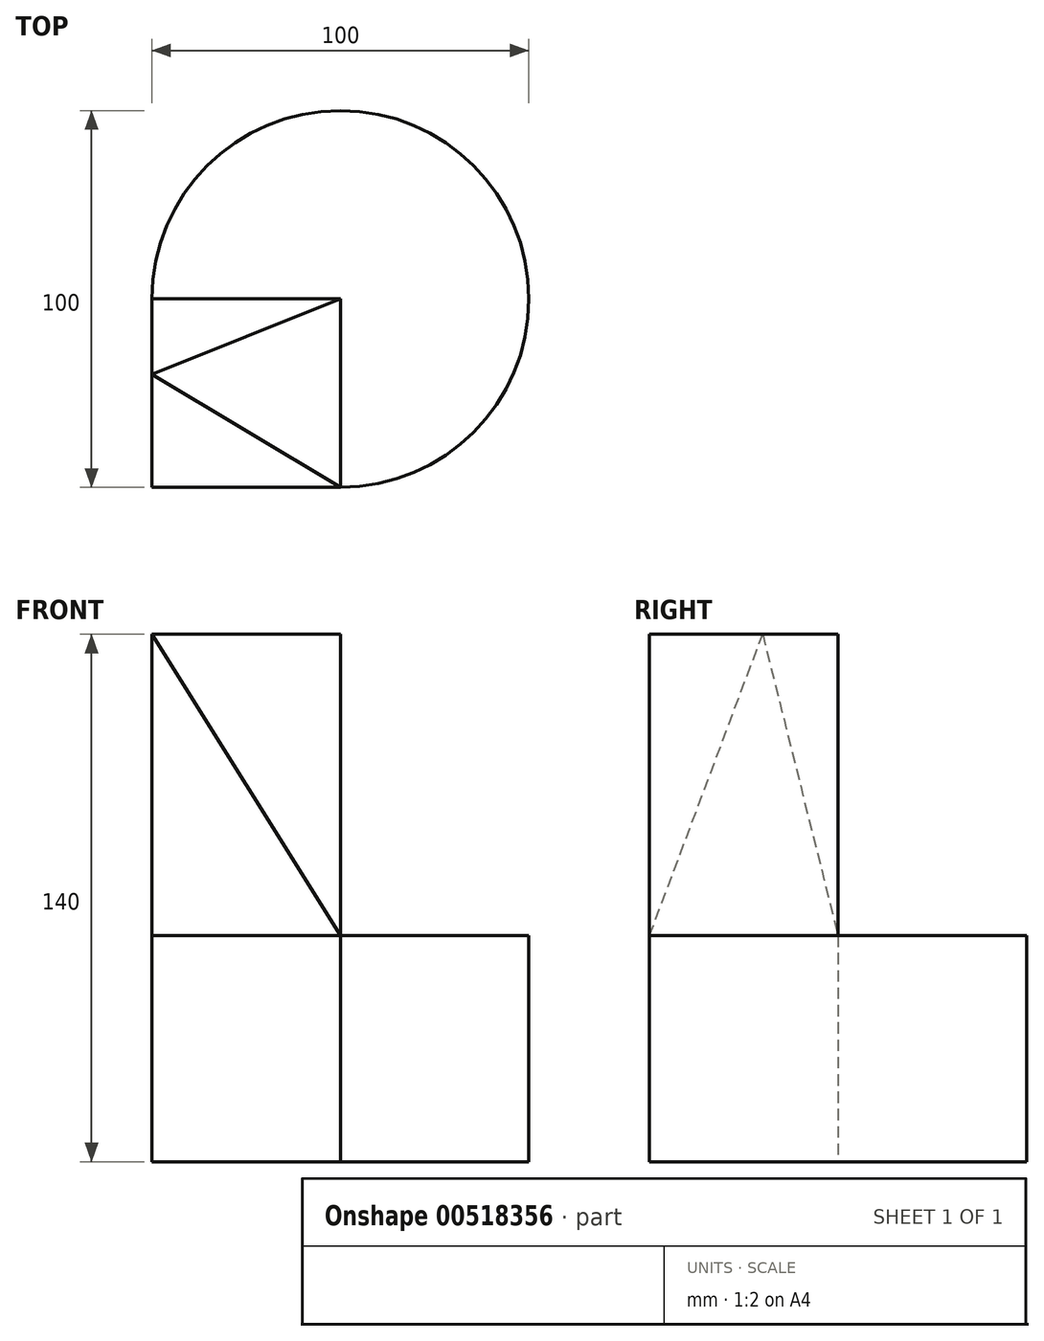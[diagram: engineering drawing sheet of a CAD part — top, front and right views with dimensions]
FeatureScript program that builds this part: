
annotation { "Feature Type Name" : "Feature", "Feature Type Description" : "" }
export const myFeature = defineFeature(function(context is Context, id is Id, definition is map)
    precondition{}
    {
        {
            var Q0;
            Q0=qCreatedBy(makeId("Top.planeOp"),FACE);
            var sketch = newSketch(context, id + "F0", { "sketchPlane" : qUnion([Q0])});
            skCircle(sketch, "E0", {"center": v(0, 0) * mm, "radius": 50 * mm});
            skSolve(sketch);
        }
        {
            var Q0;
            Q0 = qSketchRegion(id + "F0", true);
            extrude(context, id + "F1", {"entities" : qUnion([Q0]), "depth" : 140 * mm, "offsetDistance" : 25 * mm});
        }
        {
            var Q0;
            Q0=makeQuery(id+"F1.opExtrude","CAP_FACE",FACE,{"disambiguationData":[OSD([sQuery(id+"F0.wireOp",EDGE,"E0")])],"isStart":false});
            var sketch = newSketch(context, id + "F2", { "sketchPlane" : qUnion([Q0])});
            skLineSegment(sketch, "E1", {"start": v(0, 0) * mm, "end": v(0, 50) * mm});
            skLineSegment(sketch, "E2", {"start": v(0, 0) * mm, "end": v(0, -50) * mm});
            skSolve(sketch);
        }
        {
            var Q0;
            Q0=makeQuery(id+"F1.opExtrude","CAP_FACE",FACE,{"disambiguationData":[OSD([sQuery(id+"F0.wireOp",EDGE,"E0")])],"isStart":true});
            cPlane(context, id + "F3", {"entities" : qUnion([Q0]), "cplaneType" : CPlaneType.OFFSET, "offset" : 60 * mm, "oppositeDirection" : true, "width" : 150 * mm, "height" : 150 * mm});
        }
        {
            var Q0;
            {var subQ0=sQuery(id+"F2.wireOp",EDGE,"E1");Q0=makeQuery(id+"F2.imprint","IMPRINT",FACE,{"disambiguationData":[TD([[makeQuery(id+"F2.imprint","IMPRINT",EDGE,{"derivedFrom":subQ0}),-1.0]])]});}
            var Q1;
            Q1=qCreatedBy(id+"F3.planeOp",FACE);
            extrude(context, id + "F4", {"entities" : qUnion([Q0]), "operationType" : NewBodyOperationType.REMOVE, "endBound" : BoundingType.UP_TO_SURFACE, "oppositeDirection" : true, "depth" : 25 * mm, "endBoundEntityFace" : qUnion([Q1]), "offsetDistance" : 25 * mm});
        }
        {
            var Q0;
            Q0=makeQuery(id+"F1.opExtrude","CAP_FACE",FACE,{"disambiguationData":[OSD([sQuery(id+"F0.wireOp",EDGE,"E0")])],"isStart":false});
            var sketch = newSketch(context, id + "F5", { "sketchPlane" : qUnion([Q0])});
            skLineSegment(sketch, "E3", {"start": v(0, 0) * mm, "end": v(-50, 0) * mm});
            skSolve(sketch);
        }
        {
            var Q0;
            {var subQ0=sQuery(id+"F5.wireOp",EDGE,"E3");Q0=makeQuery(id+"F5.imprint","IMPRINT",FACE,{"disambiguationData":[TD([[makeQuery(id+"F5.imprint","IMPRINT",EDGE,{"derivedFrom":subQ0}),-1.0]])]});}
            var Q1;
            Q1=qCreatedBy(id+"F3.planeOp",FACE);
            extrude(context, id + "F6", {"entities" : qUnion([Q0]), "operationType" : NewBodyOperationType.REMOVE, "endBound" : BoundingType.UP_TO_SURFACE, "oppositeDirection" : true, "depth" : 25 * mm, "endBoundEntityFace" : qUnion([Q1]), "offsetDistance" : 25 * mm});
        }
        {
            var Q0;
            Q0=makeQuery(id+"F1.opExtrude","CAP_FACE",FACE,{"disambiguationData":[OSD([sQuery(id+"F0.wireOp",EDGE,"E0")])],"isStart":false});
            var Q1;
            Q1=qCreatedBy(id+"F3.planeOp",FACE);
            extrude(context, id + "F7", {"entities" : qUnion([Q0]), "operationType" : NewBodyOperationType.REMOVE, "endBound" : BoundingType.UP_TO_SURFACE, "oppositeDirection" : true, "depth" : 25 * mm, "endBoundEntityFace" : qUnion([Q1]), "offsetDistance" : 25 * mm});
        }
        {
            var Q0;
            {var subQ0=sQuery(id+"F0.wireOp",EDGE,"E0");var subQ1=sQuery(id+"F2.wireOp",EDGE,"E2");var subQ2=sQuery(id+"F2.wireOp",EDGE,"E1");Q0=makeQuery(id+"F7.boolean.opBoolean","MERGE",FACE,{"derivedFrom":[makeQuery(id+"F6.boolean.opBoolean","MERGE",FACE,{"derivedFrom":[makeQuery(id+"F4.boolean.opBoolean","COPY",FACE,{"derivedFrom":makeQuery(id+"F4.opExtrude","CAP_FACE",FACE,{"disambiguationData":[OSD([subQ0,subQ2,subQ1])],"isStart":false})})],"fromTools":[makeQuery(id+"F6.opExtrude","CAP_FACE",FACE,{"disambiguationData":[OSD([subQ0,subQ2,subQ1,sQuery(id+"F5.wireOp",EDGE,"E3")])],"isStart":false})]})],"fromTools":[makeQuery(id+"F7.opExtrude","CAP_FACE",FACE,{"disambiguationData":[OSD([subQ0])],"isStart":false})]});}
            var sketch = newSketch(context, id + "F8", { "sketchPlane" : qUnion([Q0])});
            skLineSegment(sketch, "E4.bottom", {"start": v(0, 0) * mm, "end": v(-50, 0) * mm});
            skLineSegment(sketch, "E4.top", {"start": v(0, -50) * mm, "end": v(-50, -50) * mm});
            skLineSegment(sketch, "E4.left", {"start": v(0, 0) * mm, "end": v(0, -50) * mm});
            skLineSegment(sketch, "E4.right", {"start": v(-50, 0) * mm, "end": v(-50, -50) * mm});
            skSolve(sketch);
        }
        {
            var Q0;
            Q0=makeQuery(id+"F1.opExtrude","CAP_FACE",FACE,{"disambiguationData":[OSD([sQuery(id+"F0.wireOp",EDGE,"E0")])],"isStart":true});
            cPlane(context, id + "F9", {"entities" : qUnion([Q0]), "cplaneType" : CPlaneType.OFFSET, "offset" : 140 * mm, "oppositeDirection" : true, "width" : 150 * mm, "height" : 150 * mm});
        }
        {
            var Q0;
            Q0 = qSketchRegion(id + "F8", true);
            var Q1;
            Q1=qCreatedBy(id+"F9.planeOp",FACE);
            extrude(context, id + "F10", {"entities" : qUnion([Q0]), "operationType" : NewBodyOperationType.ADD, "endBound" : BoundingType.UP_TO_SURFACE, "depth" : 25 * mm, "endBoundEntityFace" : qUnion([Q1]), "offsetDistance" : 25 * mm});
        }
        {
            var Q0;
            Q0=makeQuery(id+"F10.opExtrude","CAP_FACE",FACE,{"disambiguationData":[OSD([sQuery(id+"F8.wireOp",EDGE,"E4.bottom"),sQuery(id+"F8.wireOp",EDGE,"E4.top"),sQuery(id+"F8.wireOp",EDGE,"E4.left"),sQuery(id+"F8.wireOp",EDGE,"E4.right")])],"isStart":false});
            var sketch = newSketch(context, id + "F11", { "sketchPlane" : qUnion([Q0])});
            skLineSegment(sketch, "E5", {"start": v(-50, -20) * mm, "end": v(0, 0) * mm});
            skLineSegment(sketch, "E6", {"start": v(0, 0) * mm, "end": v(0, -50) * mm});
            skLineSegment(sketch, "E7", {"start": v(0, -50) * mm, "end": v(-50, -20) * mm});
            skSolve(sketch);
        }
        {
            var Q0;
            Q0=makeQuery(id+"F10.opExtrude","SWEPT_FACE",FACE,{"disambiguationData":[OSD([sQuery(id+"F8.wireOp",EDGE,"E4.left")])]});
            var sketch = newSketch(context, id + "F12", { "sketchPlane" : qUnion([Q0])});
            skLineSegment(sketch, "E8", {"start": v(-20, 140) * mm, "end": v(-50, 60) * mm});
            skLineSegment(sketch, "E9", {"start": v(-50, 60) * mm, "end": v(0, 60) * mm});
            skLineSegment(sketch, "E10", {"start": v(0, 60) * mm, "end": v(-20, 140) * mm});
            skSolve(sketch);
        }
        {
            var Q1;
            {var subQ0=sQuery(id+"F11.wireOp",EDGE,"E5");Q1=makeQuery(id+"F11.imprint","IMPRINT",FACE,{"disambiguationData":[TD([[makeQuery(id+"F11.imprint","IMPRINT",EDGE,{"derivedFrom":subQ0}),1.0]])]});}
            var Q2;
            Q2=sQuery(id+"F12.wireOp",VERTEX,"E10.start");
            loft(context, id + "F13", {"operationType" : NewBodyOperationType.REMOVE, "sheetProfilesArray" : [{ "sheetProfileEntities" : qUnion([Q1]) }, { "sheetProfileEntities" : qUnion([Q2]) }]});
        }
        {
            var Q1;
            Q1=makeQuery(id+"F10.opExtrude","SWEPT_FACE",FACE,{"disambiguationData":[OSD([sQuery(id+"F8.wireOp",EDGE,"E4.top")])]});
            var Q2;
            Q2=makeQuery(id+"F13.boolean.opBoolean","COPY",VERTEX,{"derivedFrom":makeQuery(id+"F13.opLoft","MID_CAP_VERTEX",VERTEX,{"disambiguationData":[OSD([sQuery(id+"F8.wireOp",EDGE,"E4.right"),dummyQuery(id+"F9.planeOp",FACE),sQuery(id+"F11.wireOp",EDGE,"E5"),sQuery(id+"F11.wireOp",EDGE,"E7")])],"capPos":0.0})});
            loft(context, id + "F14", {"operationType" : NewBodyOperationType.REMOVE, "sheetProfilesArray" : [{ "sheetProfileEntities" : qUnion([Q1]) }, { "sheetProfileEntities" : qUnion([Q2]) }]});
        }
        {
            var Q0;
            Q0=makeQuery(id+"F1.opExtrude","CAP_FACE",FACE,{"disambiguationData":[OSD([sQuery(id+"F0.wireOp",EDGE,"E0")])],"isStart":true});
            var sketch = newSketch(context, id + "F15", { "sketchPlane" : qUnion([Q0])});
            skLineSegment(sketch, "E11", {"start": v(0, 50) * mm, "end": v(0, 0) * mm});
            skLineSegment(sketch, "E12", {"start": v(0, 0) * mm, "end": v(-50, 0) * mm});
            skSolve(sketch);
        }
        {
            var Q0;
            {var subQ0=sQuery(id+"F15.wireOp",EDGE,"E11");Q0=makeQuery(id+"F15.imprint","IMPRINT",FACE,{"disambiguationData":[TD([[makeQuery(id+"F15.imprint","IMPRINT",EDGE,{"derivedFrom":subQ0}),-1.0]])]});}
            var Q1;
            Q1=makeQuery(id+"F10.opExtrude","CAP_FACE",FACE,{"disambiguationData":[OSD([sQuery(id+"F8.wireOp",EDGE,"E4.bottom"),sQuery(id+"F8.wireOp",EDGE,"E4.top"),sQuery(id+"F8.wireOp",EDGE,"E4.left"),sQuery(id+"F8.wireOp",EDGE,"E4.right")])],"isStart":true});
            extrude(context, id + "F16", {"entities" : qUnion([Q0]), "operationType" : NewBodyOperationType.REMOVE, "endBound" : BoundingType.UP_TO_SURFACE, "oppositeDirection" : true, "depth" : 25 * mm, "endBoundEntityFace" : qUnion([Q1]), "offsetDistance" : 25 * mm});
        }
        {
            var Q0;
            Q0=makeQuery(id+"F10.opExtrude","CAP_FACE",FACE,{"disambiguationData":[OSD([sQuery(id+"F8.wireOp",EDGE,"E4.bottom"),sQuery(id+"F8.wireOp",EDGE,"E4.top"),sQuery(id+"F8.wireOp",EDGE,"E4.left"),sQuery(id+"F8.wireOp",EDGE,"E4.right")])],"isStart":false});
            cPlane(context, id + "F17", {"entities" : qUnion([Q0]), "cplaneType" : CPlaneType.OFFSET, "offset" : 140 * mm, "oppositeDirection" : true, "width" : 150 * mm, "height" : 150 * mm});
        }
    });
